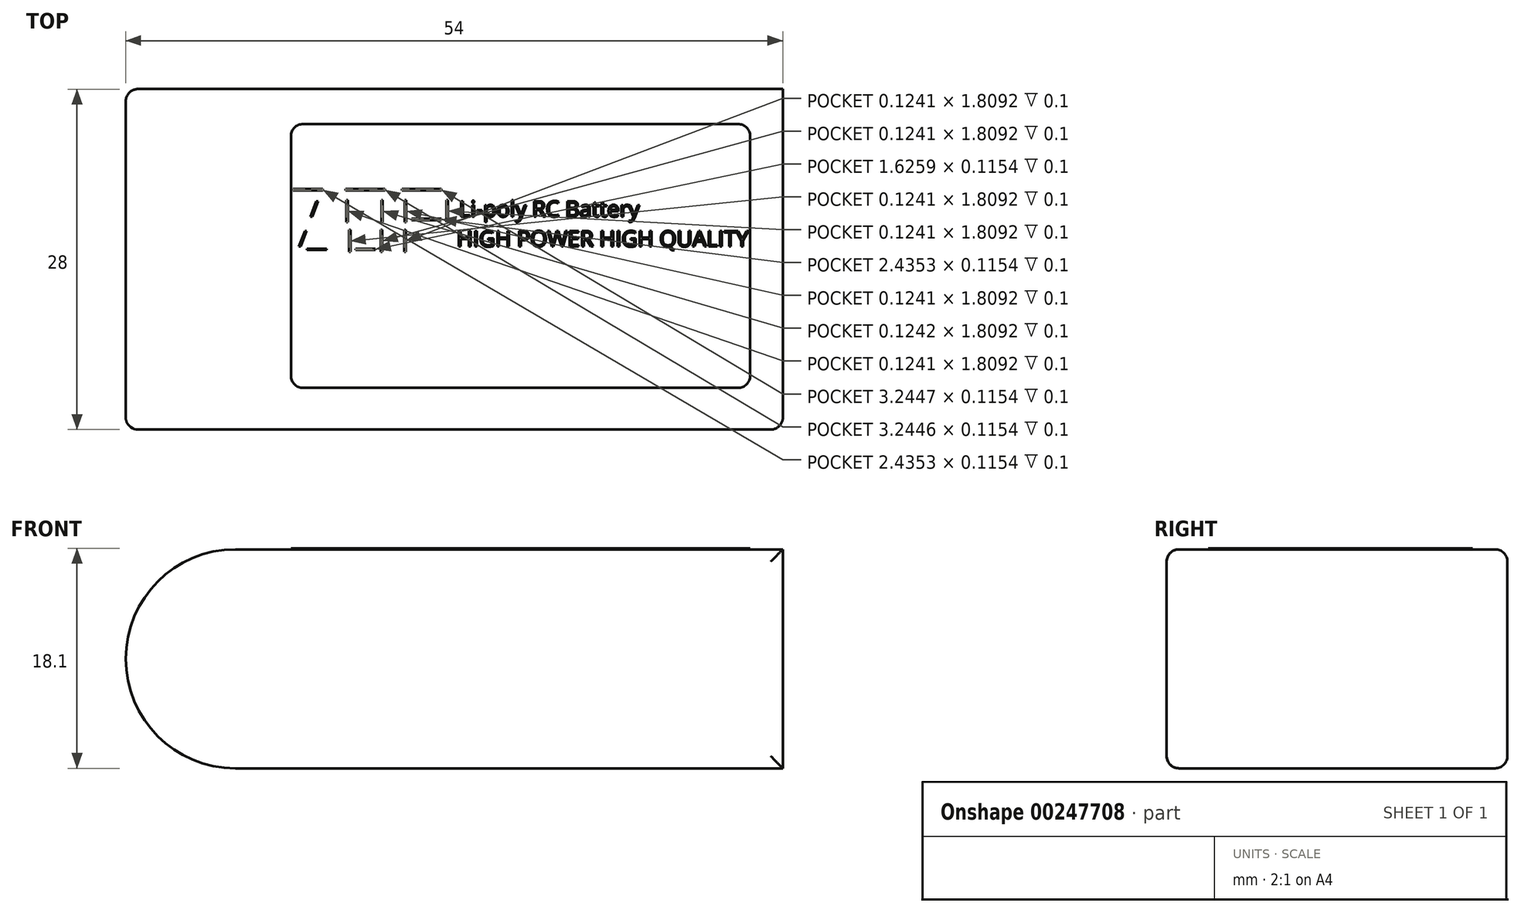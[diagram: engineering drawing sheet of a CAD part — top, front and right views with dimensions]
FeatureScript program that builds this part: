
annotation { "Feature Type Name" : "Feature", "Feature Type Description" : "" }
export const myFeature = defineFeature(function(context is Context, id is Id, definition is map)
    precondition{}
    {
        {
            var Q0;
            Q0=qCreatedBy(makeId("Top.planeOp"),FACE);
            var sketch = newSketch(context, id + "F0", { "sketchPlane" : qUnion([Q0])});
            skLineSegment(sketch, "E0.bottom", {"start": v(-30.4, 19.44) * mm, "end": v(23.6, 19.44) * mm});
            skLineSegment(sketch, "E0.top", {"start": v(-30.4, -8.56) * mm, "end": v(23.6, -8.56) * mm});
            skLineSegment(sketch, "E0.left", {"start": v(-30.4, 19.44) * mm, "end": v(-30.4, -8.56) * mm});
            skLineSegment(sketch, "E0.right", {"start": v(23.6, 19.44) * mm, "end": v(23.6, -8.56) * mm});
            skSolve(sketch);
        }
        {
            var Q0;
            Q0 = qSketchRegion(id + "F0", true);
            extrude(context, id + "F1", {"entities" : qUnion([Q0]), "depth" : 18 * mm});
        }
        {
            var Q0;
            Q0=makeQuery(id+"F1.opExtrude","CAP_EDGE",EDGE,{"disambiguationData":[OSD([sQuery(id+"F0.wireOp",EDGE,"E0.left")])],"isStart":false});
            var Q1;
            Q1=makeQuery(id+"F1.opExtrude","CAP_EDGE",EDGE,{"disambiguationData":[OSD([sQuery(id+"F0.wireOp",EDGE,"E0.left")])],"isStart":true});
            fillet(context, id + "F2", {"entities" : qUnion([Q0, Q1]), "radius" : 9 * mm, "tangentPropagation" : true, "allowEdgeOverflow" : false});
        }
        {
            var Q0;
            Q0=makeQuery(id+"F1.opExtrude","CAP_FACE",FACE,{"disambiguationData":[OSD([sQuery(id+"F0.wireOp",EDGE,"E0.bottom"),sQuery(id+"F0.wireOp",EDGE,"E0.top"),sQuery(id+"F0.wireOp",EDGE,"E0.left"),sQuery(id+"F0.wireOp",EDGE,"E0.right")])],"isStart":false});
            var sketch = newSketch(context, id + "F3", { "sketchPlane" : qUnion([Q0])});
            skText(sketch, "E1", { "text": "___    ____   ____  \n   /    |    |  |___| Li-poly RC Battery\n /__   |__|  |        HIGH POWER HIGH QUALITY", "fontName": "OpenSans-Regular.ttf"});
            skLineSegment(sketch, "E2.bottom", {"start": v(-15.83, 16.57) * mm, "end": v(19.91, 16.57) * mm});
            skLineSegment(sketch, "E2.top", {"start": v(-15.83, -5.13) * mm, "end": v(19.91, -5.13) * mm});
            skLineSegment(sketch, "E2.left", {"start": v(-16.83, 15.57) * mm, "end": v(-16.83, -4.13) * mm});
            skLineSegment(sketch, "E2.right", {"start": v(20.91, 15.57) * mm, "end": v(20.91, -4.13) * mm});
            skPoint(sketch, "E3.visualSharp", {"position": v(-16.83, 16.57) * mm});
            skArc(sketch, "E3.filletArc", {"start": v(-15.83, 16.57) * mm, "mid": v(-16.53, 16.27) * mm, "end": v(-16.83, 15.57) * mm});
            skPoint(sketch, "E4.visualSharp", {"position": v(20.91, 16.57) * mm});
            skArc(sketch, "E4.filletArc", {"start": v(20.91, 15.57) * mm, "mid": v(20.62, 16.27) * mm, "end": v(19.91, 16.57) * mm});
            skPoint(sketch, "E5.visualSharp", {"position": v(20.91, -5.13) * mm});
            skArc(sketch, "E5.filletArc", {"start": v(19.91, -5.13) * mm, "mid": v(20.62, -4.84) * mm, "end": v(20.91, -4.13) * mm});
            skPoint(sketch, "E6.visualSharp", {"position": v(-16.83, -5.13) * mm});
            skArc(sketch, "E6.filletArc", {"start": v(-16.83, -4.13) * mm, "mid": v(-16.53, -4.84) * mm, "end": v(-15.83, -5.13) * mm});
            const initialGuessF3  = {"E1": [-0.01665, 0.0114, 1, 0, 0.0013]};
            skSetInitialGuess(sketch, initialGuessF3);
            skSolve(sketch);
        }
        {
            var Q0;
            Q0=makeQuery(id+"F3.imprint","IMPRINT",FACE,{"disambiguationData":[TD([[makeQuery(id+"F3.imprint","IMPRINT",EDGE,{"derivedFrom":sQuery(id+"F3.wireOp",EDGE,"E1.sketch_text.stroke-114")}),1.0]])]});
            var Q1;
            Q1=makeQuery(id+"F3.imprint","IMPRINT",FACE,{"disambiguationData":[TD([[makeQuery(id+"F3.imprint","IMPRINT",EDGE,{"derivedFrom":sQuery(id+"F3.wireOp",EDGE,"E1.sketch_text.stroke-132")}),1.0]])]});
            var Q2;
            Q2=makeQuery(id+"F3.imprint","IMPRINT",FACE,{"disambiguationData":[TD([[makeQuery(id+"F3.imprint","IMPRINT",EDGE,{"derivedFrom":sQuery(id+"F3.wireOp",EDGE,"E1.sketch_text.stroke-171")}),1.0]])]});
            var Q3;
            Q3=makeQuery(id+"F3.imprint","IMPRINT",FACE,{"disambiguationData":[TD([[makeQuery(id+"F3.imprint","IMPRINT",EDGE,{"derivedFrom":sQuery(id+"F3.wireOp",EDGE,"E1.sketch_text.stroke-204")}),1.0]])]});
            var Q4;
            Q4=makeQuery(id+"F3.imprint","IMPRINT",FACE,{"disambiguationData":[TD([[makeQuery(id+"F3.imprint","IMPRINT",EDGE,{"derivedFrom":sQuery(id+"F3.wireOp",EDGE,"E1.sketch_text.stroke-211")}),1.0]])]});
            var Q5;
            Q5=makeQuery(id+"F3.imprint","IMPRINT",FACE,{"disambiguationData":[TD([[makeQuery(id+"F3.imprint","IMPRINT",EDGE,{"derivedFrom":sQuery(id+"F3.wireOp",EDGE,"E1.sketch_text.stroke-237")}),1.0]])]});
            var Q6;
            Q6=makeQuery(id+"F3.imprint","IMPRINT",FACE,{"disambiguationData":[TD([[makeQuery(id+"F3.imprint","IMPRINT",EDGE,{"derivedFrom":sQuery(id+"F3.wireOp",EDGE,"E1.sketch_text.stroke-297")}),1.0]])]});
            var Q7;
            Q7=makeQuery(id+"F3.imprint","IMPRINT",FACE,{"disambiguationData":[TD([[makeQuery(id+"F3.imprint","IMPRINT",EDGE,{"derivedFrom":sQuery(id+"F3.wireOp",EDGE,"E1.sketch_text.stroke-485")}),1.0]])]});
            var Q8;
            Q8=makeQuery(id+"F3.imprint","IMPRINT",FACE,{"disambiguationData":[TD([[makeQuery(id+"F3.imprint","IMPRINT",EDGE,{"derivedFrom":sQuery(id+"F3.wireOp",EDGE,"E1.sketch_text.stroke-434")}),1.0]])]});
            var Q9;
            Q9=makeQuery(id+"F3.imprint","IMPRINT",FACE,{"disambiguationData":[TD([[makeQuery(id+"F3.imprint","IMPRINT",EDGE,{"derivedFrom":sQuery(id+"F3.wireOp",EDGE,"E1.sketch_text.stroke-419")}),1.0]])]});
            var Q10;
            Q10=makeQuery(id+"F3.imprint","IMPRINT",FACE,{"disambiguationData":[TD([[makeQuery(id+"F3.imprint","IMPRINT",EDGE,{"derivedFrom":sQuery(id+"F3.wireOp",EDGE,"E1.sketch_text.stroke-552")}),1.0]])]});
            var Q11;
            Q11=makeQuery(id+"F3.imprint","IMPRINT",FACE,{"disambiguationData":[TD([[makeQuery(id+"F3.imprint","IMPRINT",EDGE,{"derivedFrom":sQuery(id+"F3.wireOp",EDGE,"E1.sketch_text.stroke-582")}),1.0]])]});
            var Q12;
            {var subQ99=sQuery(id+"F3.wireOp",EDGE,"E1.sketch_text.stroke-0");Q12=makeQuery(id+"F3.imprint","IMPRINT",FACE,{"disambiguationData":[TD([[makeQuery(id+"F3.imprint","IMPRINT",EDGE,{"derivedFrom":subQ99}),1.0]])]});}
            extrude(context, id + "F4", {"entities" : qUnion([Q0, Q1, Q2, Q3, Q4, Q5, Q6, Q7, Q8, Q9, Q10, Q11, Q12]), "operationType" : NewBodyOperationType.ADD, "depth" : .1 * mm});
        }
        {
            var Q0;
            Q0=makeQuery(id+"F1.opExtrude","CAP_EDGE",EDGE,{"disambiguationData":[OSD([sQuery(id+"F0.wireOp",EDGE,"E0.bottom")])],"isStart":false});
            var Q1;
            Q1=makeQuery(id+"F1.opExtrude","SWEPT_FACE",FACE,{"disambiguationData":[OSD([sQuery(id+"F0.wireOp",EDGE,"E0.top")])]});
            fillet(context, id + "F5", {"entities" : qUnion([Q0, Q1]), "radius" : 1 * mm, "tangentPropagation" : true, "allowEdgeOverflow" : false});
        }
    });
